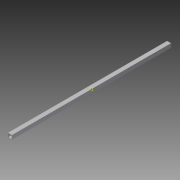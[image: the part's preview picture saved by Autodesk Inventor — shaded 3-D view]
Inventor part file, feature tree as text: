
AUTODESK INVENTOR PART (.ipt)
format: ipt  version: 2013 (Build 170138000, 138)  size: 77,312 bytes
history: native  units: in
note: dims shown in document units (in); Inventor stores cm internally (conversion verified against a paired STEP export)
features: other x3, sketch x1, plane x1
ambient origin geometry x8: Origin, YZ Plane, XZ Plane, XY Plane, X Axis, Y Axis, Z Axis, Center Point
bodies: Solid1 (feature_tree)
feature tree (5):
  other  "FE-00036Support.ipt"
  other  "Solid1::FE-00036Support.ipt"
  other  "TaggingFeature1"
  sketch  "Sketch1"  dims[d0=0.3937in d1=0.0in]
  plane  "Work Plane1"
